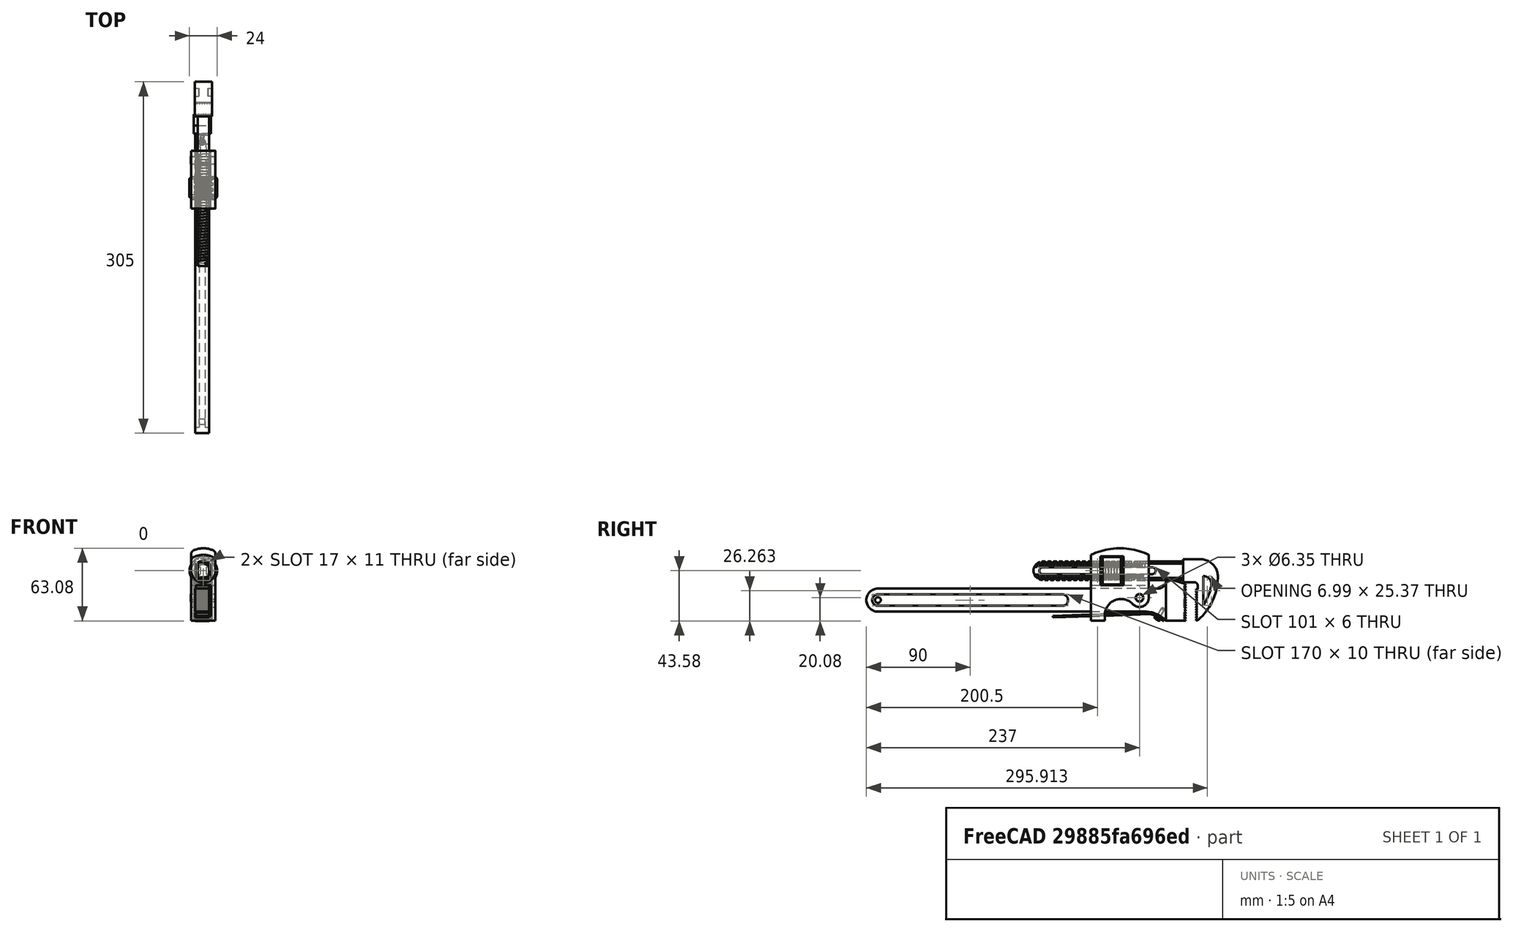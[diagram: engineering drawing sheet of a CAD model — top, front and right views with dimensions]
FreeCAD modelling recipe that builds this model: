
FCSTD DOCUMENT  (FreeCAD 0.17R13247 (Git))
Label: GRIFO CJ
License: All rights reserved
LicenseURL: http://en.wikipedia.org/wiki/All_rights_reserved
objects: App::FeaturePython×18, Part::FeaturePython×7
note: 7 computed .brp shape members not serialized (recipe doc carries the construction recipe); baked Part::Feature solids carry a one-line shape summary decoded from their .brp

FEATURE [Part::FeaturePython] MANDIBULA_FIXA_01  # a2plus imported part (geometry in sourceFile) (typed FeaturePython)
  Placement = pos=(0,0,0) rot=(1,0,0;1.5708rad)
  fixedPosition = true
  sourceFile = <path> GRIFO/MANDIBULA FIXA.FCStd
  timeLastImport = 1.52331e+09
  updateColors = true
FEATURE [Part::FeaturePython] CAPA_01  # a2plus imported part (geometry in sourceFile) (typed FeaturePython)
  Placement = pos=(1,-40,13.5) rot=(1,0,0;1.5708rad)
  fixedPosition = false
  sourceFile = <path> GRIFO/CAPA.FCStd
  timeLastImport = 1.52331e+09
  updateColors = true
FEATURE [App::FeaturePython] circularEdgeConstraint01  label="circularEdgeConstraint01__MANDIBULA_FIXA_01"  # a2plus constraint (typed FeaturePython)
  Object1 = CAPA_01
  Object2 = MANDIBULA_FIXA_01
  SubElement1 = Edge83
  SubElement2 = Edge1115
  Type = circularEdge
  directionConstraint = 0
  lockRotation = false
  offset = 0.5
FEATURE [App::FeaturePython] circularEdgeConstraint01_mirror  label="circularEdgeConstraint01__CAPA_01"  # a2plus constraint (typed FeaturePython)
  Object1 = CAPA_01
  Object2 = MANDIBULA_FIXA_01
  SubElement1 = Edge83
  SubElement2 = Edge1115
  Type = circularEdge
  directionConstraint = 0
  lockRotation = false
  offset = 0.5
FEATURE [App::FeaturePython] angleConstraint01  label="angleConstraint01__MANDIBULA_FIXA_01"  # a2plus constraint (typed FeaturePython)
  Object1 = CAPA_01
  Object2 = MANDIBULA_FIXA_01
  SubElement1 = Face31
  SubElement2 = Face385
  Type = angle_between_planes
  angle = 180
FEATURE [App::FeaturePython] angleConstraint01_mirror  label="angleConstraint01__CAPA_01"  # a2plus constraint (typed FeaturePython)
  Object1 = CAPA_01
  Object2 = MANDIBULA_FIXA_01
  SubElement1 = Face31
  SubElement2 = Face385
  Type = angle_between_planes
  angle = 180
FEATURE [Part::FeaturePython] PORCA_01  # a2plus imported part (geometry in sourceFile) (typed FeaturePython)
  Placement = pos=(1,-47,25.5) rot=(0,0,1;1.5708rad)
  fixedPosition = false
  sourceFile = <path> GRIFO/PORCA.FCStd
  timeLastImport = 1.52331e+09
  updateColors = true
FEATURE [App::FeaturePython] circularEdgeConstraint02  label="circularEdgeConstraint02__PORCA_01"  # a2plus constraint (typed FeaturePython)
  Object1 = CAPA_01
  Object2 = PORCA_01
  SubElement1 = Edge63
  SubElement2 = Edge13
  Type = circularEdge
  directionConstraint = 1
  lockRotation = false
  offset = 0.5
FEATURE [App::FeaturePython] circularEdgeConstraint02_mirror  label="circularEdgeConstraint02__CAPA_01"  # a2plus constraint (typed FeaturePython)
  Object1 = CAPA_01
  Object2 = PORCA_01
  SubElement1 = Edge63
  SubElement2 = Edge13
  Type = circularEdge
  directionConstraint = 1
  lockRotation = false
  offset = 0.5
FEATURE [Part::FeaturePython] MANDIBULA_MOVEL_01  # a2plus imported part (geometry in sourceFile) (typed FeaturePython)
  Placement = pos=(1,15,25.5) rot=(0,-0.707107,-0.707107;3.14159rad)
  fixedPosition = false
  sourceFile = <path> GRIFO/MANDIBULA MOVEL.FCStd
  timeLastImport = 1.52331e+09
  updateColors = true
FEATURE [App::FeaturePython] circularEdgeConstraint03  label="circularEdgeConstraint03__MANDIBULA_MOVEL_01"  # a2plus constraint (typed FeaturePython)
  Object1 = CAPA_01
  Object2 = MANDIBULA_MOVEL_01
  SubElement1 = Edge20
  SubElement2 = Edge1533
  Type = circularEdge
  a = 80
  a_0_animatation = 30
  a_1_animatation = 80
  a_n_animatation = 42
  animation_exp_animatation = a
  directionConstraint = 2
  interp_method_animatation = none
  lockRotation = false
  loop_animatation = true
  n_interp_animatation = 6
  offset = 30
  play_after_generate_animatation = true
  timer_ms_animatation = 25
FEATURE [App::FeaturePython] circularEdgeConstraint03_mirror  label="circularEdgeConstraint03__CAPA_01"  # a2plus constraint (typed FeaturePython)
  Object1 = CAPA_01
  Object2 = MANDIBULA_MOVEL_01
  SubElement1 = Edge20
  SubElement2 = Edge1533
  Type = circularEdge
  directionConstraint = 2
  lockRotation = false
  offset = 30
FEATURE [App::FeaturePython] angleConstraint02  label="angleConstraint02__MANDIBULA_MOVEL_01"  # a2plus constraint (typed FeaturePython)
  Object1 = MANDIBULA_FIXA_01
  Object2 = MANDIBULA_MOVEL_01
  SubElement1 = Face378
  SubElement2 = Face668
  Type = angle_between_planes
  angle = 180
FEATURE [App::FeaturePython] angleConstraint02_mirror  label="angleConstraint02__MANDIBULA_FIXA_01"  # a2plus constraint (typed FeaturePython)
  Object1 = MANDIBULA_FIXA_01
  Object2 = MANDIBULA_MOVEL_01
  SubElement1 = Face378
  SubElement2 = Face668
  Type = angle_between_planes
  angle = 180
FEATURE [Part::FeaturePython] MOLA_01  # a2plus imported part (geometry in sourceFile) (typed FeaturePython)
  Placement = pos=(0.0001191,-1.25915,-17.4319) rot=(4e-06,0.5,-0.866025;3.14158rad)
  fixedPosition = false
  sourceFile = <path> GRIFO/MOLA.FCStd
  timeLastImport = 1.52331e+09
  updateColors = true
FEATURE [App::FeaturePython] circularEdgeConstraint04  label="circularEdgeConstraint04__MANDIBULA_FIXA_01"  # a2plus constraint (typed FeaturePython)
  Object1 = MOLA_01
  Object2 = MANDIBULA_FIXA_01
  SubElement1 = Edge20
  SubElement2 = Edge1082
  Type = circularEdge
  directionConstraint = 0
  lockRotation = false
  offset = -9
FEATURE [App::FeaturePython] circularEdgeConstraint04_mirror  label="circularEdgeConstraint04__MOLA_01"  # a2plus constraint (typed FeaturePython)
  Object1 = MOLA_01
  Object2 = MANDIBULA_FIXA_01
  SubElement1 = Edge20
  SubElement2 = Edge1082
  Type = circularEdge
  directionConstraint = 0
  lockRotation = false
  offset = -9
FEATURE [App::FeaturePython] angleConstraint03  label="angleConstraint03__MOLA_01"  # a2plus constraint (typed FeaturePython)
  Object1 = MANDIBULA_FIXA_01
  Object2 = MOLA_01
  SubElement1 = Face378
  SubElement2 = Face7
  Type = angle_between_planes
  angle = 0
FEATURE [App::FeaturePython] angleConstraint03_mirror  label="angleConstraint03__MANDIBULA_FIXA_01"  # a2plus constraint (typed FeaturePython)
  Object1 = MANDIBULA_FIXA_01
  Object2 = MOLA_01
  SubElement1 = Face378
  SubElement2 = Face7
  Type = angle_between_planes
  angle = 0
FEATURE [Part::FeaturePython] ScrewTap  label="M8x20.0-ScrewTap"  # Fasteners workbench fastener (typed FeaturePython)
  Placement = pos=(-8.5,-23,2) rot=(0,-1,0;1.5708rad)
  diameter = 9
  invert = false
  length = 20
  matchOuter = false
  offset = 0
  thread = false
FEATURE [App::FeaturePython] circularEdgeConstraint05  label="circularEdgeConstraint05__M8x20.0-ScrewTap"  # a2plus constraint (typed FeaturePython)
  Object1 = CAPA_01
  Object2 = ScrewTap
  SubElement1 = Edge35
  SubElement2 = Edge2
  Type = circularEdge
  directionConstraint = 0
  lockRotation = false
  offset = 0
FEATURE [App::FeaturePython] circularEdgeConstraint05_mirror  label="circularEdgeConstraint05__CAPA_01"  # a2plus constraint (typed FeaturePython)
  Object1 = CAPA_01
  Object2 = ScrewTap
  SubElement1 = Edge35
  SubElement2 = Edge2
  Type = circularEdge
  directionConstraint = 0
  lockRotation = false
  offset = 0
FEATURE [Part::FeaturePython] Screw  label="M3x8-Screw"  # Fasteners workbench fastener (typed FeaturePython)
  Placement = pos=(0.000129903,-6.8303,-15.0814) rot=(1,2.9e-05,0;2.61799rad)
  diameter = 4
  invert = false
  length = 3
  matchOuter = false
  offset = 0
  thread = false
  type = 16
FEATURE [App::FeaturePython] circularEdgeConstraint06  label="circularEdgeConstraint06__MOLA_01"  # a2plus constraint (typed FeaturePython)
  Object1 = Screw
  Object2 = MOLA_01
  SubElement1 = Edge2
  SubElement2 = Edge20
  Type = circularEdge
  directionConstraint = 1
  lockRotation = false
  offset = 0
FEATURE [App::FeaturePython] circularEdgeConstraint06_mirror  label="circularEdgeConstraint06__M3x8-Screw"  # a2plus constraint (typed FeaturePython)
  Object1 = Screw
  Object2 = MOLA_01
  SubElement1 = Edge2
  SubElement2 = Edge20
  Type = circularEdge
  directionConstraint = 1
  lockRotation = false
  offset = 0
note: 5 file-system paths scrubbed to <path> (originals preserved in the JSON sidecar)
